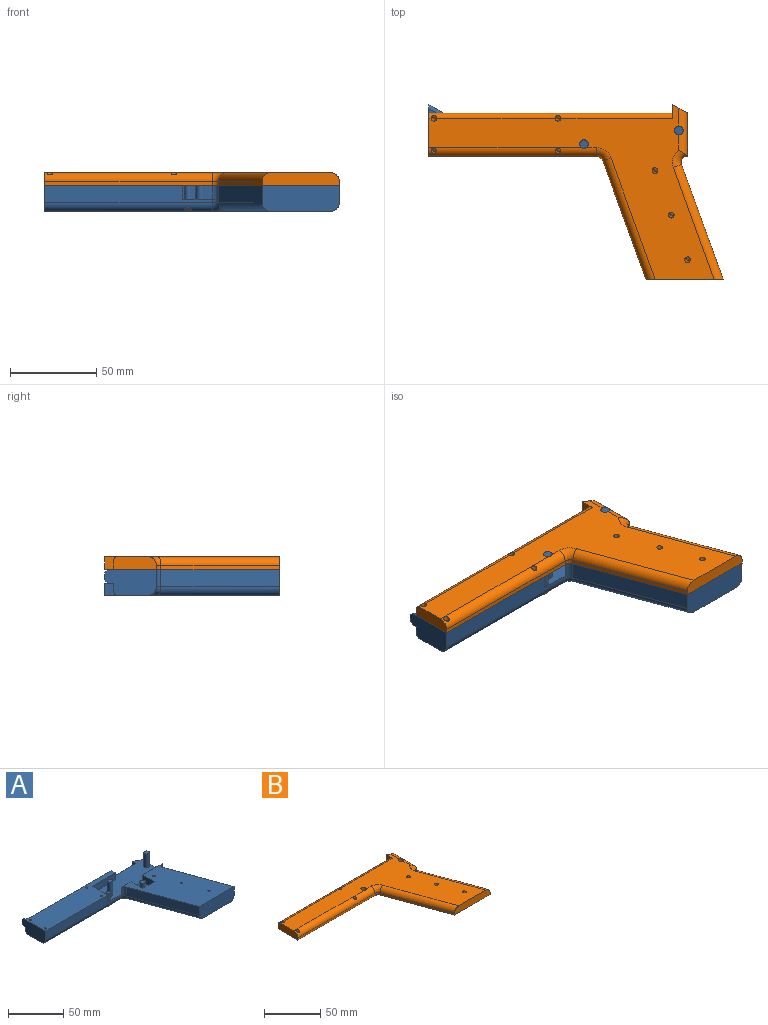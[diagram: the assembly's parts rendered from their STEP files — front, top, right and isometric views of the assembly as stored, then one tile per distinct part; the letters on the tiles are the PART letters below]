
ASSEMBLY  parts=2 mates=1
PART A: 67 faces, bbox 171.5x103.9x23.3 mm
  f0: plane 73.58x71.42mm, normal (0,0,1), area 2971.5mm2, adj f1,f5,f54,f55,f56,f57,f58,f59
  f1: plane 15x7.5mm, normal (-1,0,0), area 112.5mm2, adj f0,f2,f58,f60
  f2: plane 15x15mm, normal (0,0,1), area 205.4mm2, adj f1,f3,f58,f59,f60
  f3: cylinder r=2.5mm len=7.5mm, axis (0,0,-1), area 117.8mm2, adj f2,f4
  f4: plane 5x5mm, normal (0,0,1), area 19.6mm2, adj f3
  f5: cylinder r=3.5mm len=10mm, axis (0,0,-1), area 67.2mm2, adj f0,f6,f53,f54,f58
  f6: torus R=8.5mm, axis (0,0,1), area 67.7mm2, adj f5,f7,f8,f9,f52
  f7: cylinder r=5mm len=68.43mm, axis (-0.34,0.94,0), area 550.5mm2, adj f6,f52,f54,f55
  f8: cylinder r=5mm len=1.44mm, axis (1,0,0), area 0.2mm2, adj f6,f9,f53
  f9: cylinder r=5mm len=27.89mm, axis (0,1,0), area 182.8mm2, adj f6,f8,f10,f50,f51,f52
  f10: plane 25x2mm, normal (1,0,0), area 50mm2, adj f9,f11,f50,f53
  f11: plane 70x30mm, normal (0,0,1), area 1571.4mm2, adj f10,f12,f39,f40,f41,f42,f43,f44
  f12: plane 141.34x12mm, normal (0,1,0), area 1384.1mm2, adj f11,f13,f22,f23,f24,f25,f26,f38
  f13: plane 110x27.69mm, normal (0,0,1), area 2143.7mm2, adj f12,f14,f16,f18,f20,f22,f26,f40
  f14: cylinder r=1mm len=7.5mm, axis (0,0,-1), area 47.1mm2, adj f13,f15
  f15: plane 2x2mm, normal (0,0,1), area 3.1mm2, adj f14
  f16: cylinder r=1mm len=7.5mm, axis (0,0,-1), area 47.1mm2, adj f13,f17
  f17: plane 2x2mm, normal (0,0,1), area 3.1mm2, adj f16
  f18: cylinder r=1mm len=7.5mm, axis (0,0,-1), area 47.1mm2, adj f13,f19
  f19: plane 2x2mm, normal (0,0,1), area 3.1mm2, adj f18
  f20: cylinder r=1mm len=7.5mm, axis (0,0,-1), area 47.1mm2, adj f13,f21
  f21: plane 2x2mm, normal (0,0,1), area 3.1mm2, adj f20
  f22: plane 8.66x5mm, normal (0.35,0.61,0.71), area 21.8mm2, adj f12,f13,f23,f26
  f23: plane 8.66x5mm, normal (0.5,0.87,0), area 40mm2, adj f12,f22,f24,f26
  f24: plane 8.66x5mm, normal (0.35,0.61,-0.71), area 21.8mm2, adj f12,f23,f25,f26
  f25: plane 4.66x2.69mm, normal (0,0,-1), area 6.3mm2, adj f12,f24,f26
  f26: plane 30x15mm, normal (-1,0,0), area 403.1mm2, adj f12,f13,f22,f23,f24,f25,f27,f38
  f27: cylinder r=5mm len=97.2mm, axis (1,0,0), area 747.2mm2, adj f26,f28,f29,f31,f32,f33,f34,f35
  f28: bspline ~2.48x1.42mm, area 1.8mm2, adj f27,f29,f34
  f29: bspline ~2.7x0.76mm, area 0.9mm2, adj f27,f28,f30,f31
  f30: plane 1.16x0.6mm, normal (0,0,-1), area 0.4mm2, adj f29,f32,f34
  f31: bspline ~2.48x1.42mm, area 1.8mm2, adj f27,f29,f32
  f32: bspline ~3.06x2.4mm, area 3.4mm2, adj f27,f30,f31,f33
  f33: bspline ~3.02x2.82mm, area 4.3mm2, adj f27,f32,f34
  f34: bspline ~3.12x2.5mm, area 3.4mm2, adj f27,f28,f30,f33
  f35: torus R=9mm, axis (0,0,1), area 55.8mm2, adj f27,f36,f52,f57
  f36: cylinder r=5mm len=72.21mm, axis (0.34,-0.94,0), area 582.1mm2, adj f35,f52,f55,f56
  f37: cylinder r=2.45mm len=2.83mm, axis (0,0,-1), area 0mm2, adj f27,f52
  f38: cylinder r=3mm len=141.34mm, axis (-1,0,0), area 666mm2, adj f12,f26,f39,f52
  f39: plane 8x7mm, normal (-1,0,0), area 36.9mm2, adj f11,f12,f38,f50,f52
  f40: plane 97.2x10mm, normal (0,-1,0), area 834.4mm2, adj f11,f13,f26,f27,f41,f57
  f41: plane 20x8mm, normal (1,0,0), area 160mm2, adj f11,f13,f40,f42
  f42: plane 30x8mm, normal (0,-1,0), area 240mm2, adj f11,f13,f41,f43
  f43: plane 8x5mm, normal (1,0,0), area 40mm2, adj f11,f12,f13,f42
  f44: cylinder r=2.45mm len=15.5mm, axis (0,0,-1), area 238.6mm2, adj f11,f45
  f45: plane 4.9x4.9mm, normal (0,0,1), area 18.9mm2, adj f44
  f46: cylinder r=2.45mm len=15.5mm, axis (0,0,-1), area 238.6mm2, adj f11,f47
  f47: plane 4.9x4.9mm, normal (0,0,1), area 18.9mm2, adj f46
  f48: cylinder r=2mm len=8mm, axis (0,0,-1), area 100.5mm2, adj f11,f49
  f49: plane 4x4mm, normal (0,0,1), area 12.6mm2, adj f48
  f50: plane 8.66x7mm, normal (0.5,0.87,0), area 63.8mm2, adj f9,f10,f11,f39,f52
  f51: cylinder r=2.45mm len=4.9mm, axis (0,0,-1), area 2.4mm2, adj f9,f52
  f52: plane 165.46x101.42mm, normal (0,0,-1), area 5149mm2, adj f6,f7,f9,f26,f27,f35,f36,f37
  f53: plane 2x0.21mm, normal (0,-1,0), area 0.4mm2, adj f5,f8,f10,f11
  f54: plane 66.72x24.28mm, normal (0.94,0.34,0), area 710mm2, adj f0,f5,f7,f55
  f55: plane 45.56x15.77mm, normal (0,-1,0), area 660.4mm2, adj f0,f7,f36,f52,f54,f56
  f56: plane 68.78x25.04mm, normal (-0.94,-0.34,0), area 732mm2, adj f0,f36,f55,f57
  f57: cylinder r=4mm len=10mm, axis (0,0,-1), area 48.9mm2, adj f0,f35,f40,f56,f58
  f58: plane 52.59x8mm, normal (0,1,0), area 308.2mm2, adj f0,f1,f2,f5,f11,f57,f59
  f59: plane 15x7.5mm, normal (1,0,0), area 112.5mm2, adj f0,f2,f58,f60
  f60: plane 15x7.5mm, normal (0,1,0), area 112.5mm2, adj f0,f1,f2,f59
  f61: cylinder r=1mm len=7.5mm, axis (0,0,-1), area 47.1mm2, adj f0,f62
  f62: plane 2x2mm, normal (0,0,1), area 3.1mm2, adj f61
  f63: cylinder r=1mm len=7.5mm, axis (0,0,-1), area 47.1mm2, adj f0,f64
  f64: plane 2x2mm, normal (0,0,1), area 3.1mm2, adj f63
  f65: cylinder r=1mm len=7.5mm, axis (0,0,-1), area 47.1mm2, adj f0,f66
  f66: plane 2x2mm, normal (0,0,1), area 3.1mm2, adj f65
PART B: 38 faces, bbox 170.8x103.1x8.6 mm
  f0: plane 25x2.5mm, normal (1,0,0), area 62.5mm2, adj f1,f11,f13,f34
  f1: plane 8.66x7.5mm, normal (0.5,0.87,0), area 68.8mm2, adj f0,f2,f12,f13,f34
  f2: plane 8x7.5mm, normal (-1,0,0), area 39.4mm2, adj f1,f3,f12,f13,f37
  f3: plane 141.34x4.5mm, normal (0,1,0), area 636mm2, adj f2,f4,f13,f37
  f4: plane 25x7.5mm, normal (-1,0,0), area 180.2mm2, adj f3,f5,f12,f13,f32,f37
  f5: plane 97.2x2.5mm, normal (0,-1,0), area 243mm2, adj f4,f6,f13,f32
  f6: cylinder r=4mm len=3.76mm, axis (0,0,-1), area 12.2mm2, adj f5,f7,f13,f31
  f7: plane 68.78x25.04mm, normal (-0.94,-0.34,0), area 183mm2, adj f6,f8,f13,f30
  f8: plane 44.79x7.5mm, normal (0,-1,0), area 324.5mm2, adj f7,f9,f12,f13,f30,f33
  f9: plane 66.72x24.28mm, normal (0.94,0.34,0), area 177.5mm2, adj f8,f10,f13,f33
  f10: cylinder r=3.5mm len=4.7mm, axis (0,0,-1), area 16.8mm2, adj f9,f11,f13,f35
  f11: plane 2.5x0.21mm, normal (0,-1,0), area 0.5mm2, adj f0,f10,f13,f36
  f12: plane 165.46x101.42mm, normal (0,0,1), area 5076.1mm2, adj f1,f2,f4,f8,f14,f15,f24,f25
  f13: plane 170.78x101.42mm, normal (0,0,-1), area 6929mm2, adj f0,f1,f2,f3,f4,f5,f6,f7
  f14: cylinder r=2.5mm len=7.5mm, axis (0,0,-1), area 117.8mm2, adj f12,f13,f32
  f15: cylinder r=2.5mm len=7.5mm, axis (0,0,-1), area 115.2mm2, adj f12,f13,f34
  f16: cylinder r=0.65mm len=1.5mm, axis (0,0,-1), area 6.1mm2, adj f13,f28
  f17: cylinder r=0.65mm len=1.5mm, axis (0,0,-1), area 6.1mm2, adj f13,f29
  f18: cylinder r=0.65mm len=1.5mm, axis (0,0,-1), area 6.1mm2, adj f13,f24
  f19: cylinder r=0.65mm len=1.5mm, axis (0,0,-1), area 6.1mm2, adj f13,f23
  f20: cylinder r=0.65mm len=1.5mm, axis (0,0,-1), area 6.1mm2, adj f13,f25
  f21: cylinder r=0.65mm len=1.5mm, axis (0,0,-1), area 6.1mm2, adj f13,f26
  f22: cylinder r=0.65mm len=1.5mm, axis (0,0,-1), area 6.1mm2, adj f13,f27
  f23: cone r=1.65mm half-angle=9.5deg, axis (0,0,1), area 38.4mm2, adj f19,f32
  f24: cone r=1.65mm half-angle=9.5deg, axis (0,0,1), area 42.8mm2, adj f12,f18,f37
  f25: cone r=1.65mm half-angle=9.5deg, axis (0,0,1), area 42.8mm2, adj f12,f20,f37
  f26: cone r=1.65mm half-angle=9.5deg, axis (0,0,1), area 38.4mm2, adj f21,f32
  f27: cone r=1.65mm half-angle=9.5deg, axis (0,0,1), area 44mm2, adj f12,f22
  f28: cone r=1.65mm half-angle=9.5deg, axis (0,0,1), area 44mm2, adj f12,f16
  f29: cone r=1.65mm half-angle=9.5deg, axis (0,0,1), area 44mm2, adj f12,f17
  f30: cylinder r=5mm len=72.21mm, axis (-0.34,0.94,0), area 580.1mm2, adj f7,f8,f12,f31
  f31: torus R=9mm, axis (0,0,1), area 55.8mm2, adj f6,f12,f30,f32
  f32: cylinder r=5mm len=97.2mm, axis (-1,0,0), area 745.5mm2, adj f4,f5,f12,f14,f23,f26,f31
  f33: cylinder r=5mm len=68.43mm, axis (0.34,-0.94,0), area 552.5mm2, adj f8,f9,f12,f35
  f34: cylinder r=5mm len=27.89mm, axis (0,-1,0), area 183.1mm2, adj f0,f1,f12,f15,f35,f36
  f35: torus R=8.5mm, axis (0,0,1), area 66.9mm2, adj f10,f12,f33,f34,f36
  f36: cylinder r=5mm len=1.44mm, axis (-1,0,0), area 0.2mm2, adj f11,f34,f35
  f37: cylinder r=3mm len=141.34mm, axis (1,0,0), area 657.6mm2, adj f2,f3,f4,f12,f24,f25
PLACE A t=(-93.77,1.24,48.7)mm
PLACE B t=(-93.77,1.24,63.7)mm
MATE fastened B.f13 <-> A.f0  axis (0,0,-1) through (-95.38,-70.18,63.7)mm
